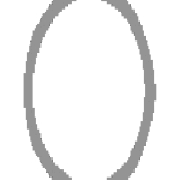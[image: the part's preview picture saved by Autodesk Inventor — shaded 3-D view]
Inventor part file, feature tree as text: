
AUTODESK INVENTOR PART (.ipt)
format: ipt  version: 2021 (Build 250183000, 183)  size: 109,056 bytes
history: native  units: in
note: dims shown in document units (in); Inventor stores cm internally (conversion verified against a paired STEP export)
features: other x4, sketch x3, plane x1
ambient origin geometry x8: Origin, YZ Plane, XZ Plane, XY Plane, X Axis, Y Axis, Z Axis, Center Point
bodies: Solid1 (feature_tree), Body (feature_tree)
feature tree (8):
  other  "Driven Length"
  other  "Frame Generator"
  other  "Start Plane"
  other  "End Plane"
  sketch  "Sketch"  dims[d2=25.5539in d4=-0.0in d5=25.5539in d6=0.12in d7=0.0in d8=90.0deg d9=25.5539in]
  sketch  "Sketch2"  dims[d0=1.0in]
  plane  "Work Plane3"
  sketch  "Sketch3"  dims[d1=0.065in]
